# Revit family: ARBOR LED BOLLARD
name_source: partatom
category: Lighting Fixtures
units: mm (PartAtom-declared; Revit-internal decimal feet)

## family parameters
Cut with Voids When Loaded = No
Host = Face
Light Source = Yes
Part Type = Normal
Room Calculation Point = No
Round Connector Dimension = Use Diameter
Shared = No

## types (1)
- ARBD
    Apparent Load = 0 VA
    Average life based on L70(HRS) = 100000
    Body Material = die cast aluminum
    CCT = 3000K,4000K
    CRI = 80
    Color Filter = 16777215
    Color Option Available = 3000K,4000K
    Default Elevation = 48 "
    Description = The Arbor led bollard has attractively shielded light distribution.  It's fully shielded light source 
effectively contains upward light spill for safety and comfort of passers by. Superior UV powder 
coating, quality die cast aluminum body, tempered safety glass lens, molded silicone gasket and 
stainless steel screws. Distinctive wood texture finish also available This bollard is an excellent 
choice for walkways, entrances, promenades, plazas, courtyards, driveways, bridges, and 
landscaped areas.
    Dimming Lamp Color Temperature Shift = <None>
    Finish/Color = wood
    Fixture Height = 31.5 "
    Fixture Width = 3.94 "
    LIGHT LENGTH = 4.92 "
    Lamp = LED
    Manufacturer = Above All Lighting
    Model = ARBD
    Photometric Web File = ARBDXXH_10301_BK.ies
    Suspenders Distance = 7.95 "
    Tilt Angle = 90.00°
    Type Comments = ARBOR LED BOLLARD
    URL = https://www.abovealllighting.com
    Voltage = 277 V
    Voltage Comments = 120-277V
    Wattage Comments = 10W
    light width = 3.54 "

## geometry (parser evidence)
native form markers: Sweep x2
no freeform markers — native parametric forms only
